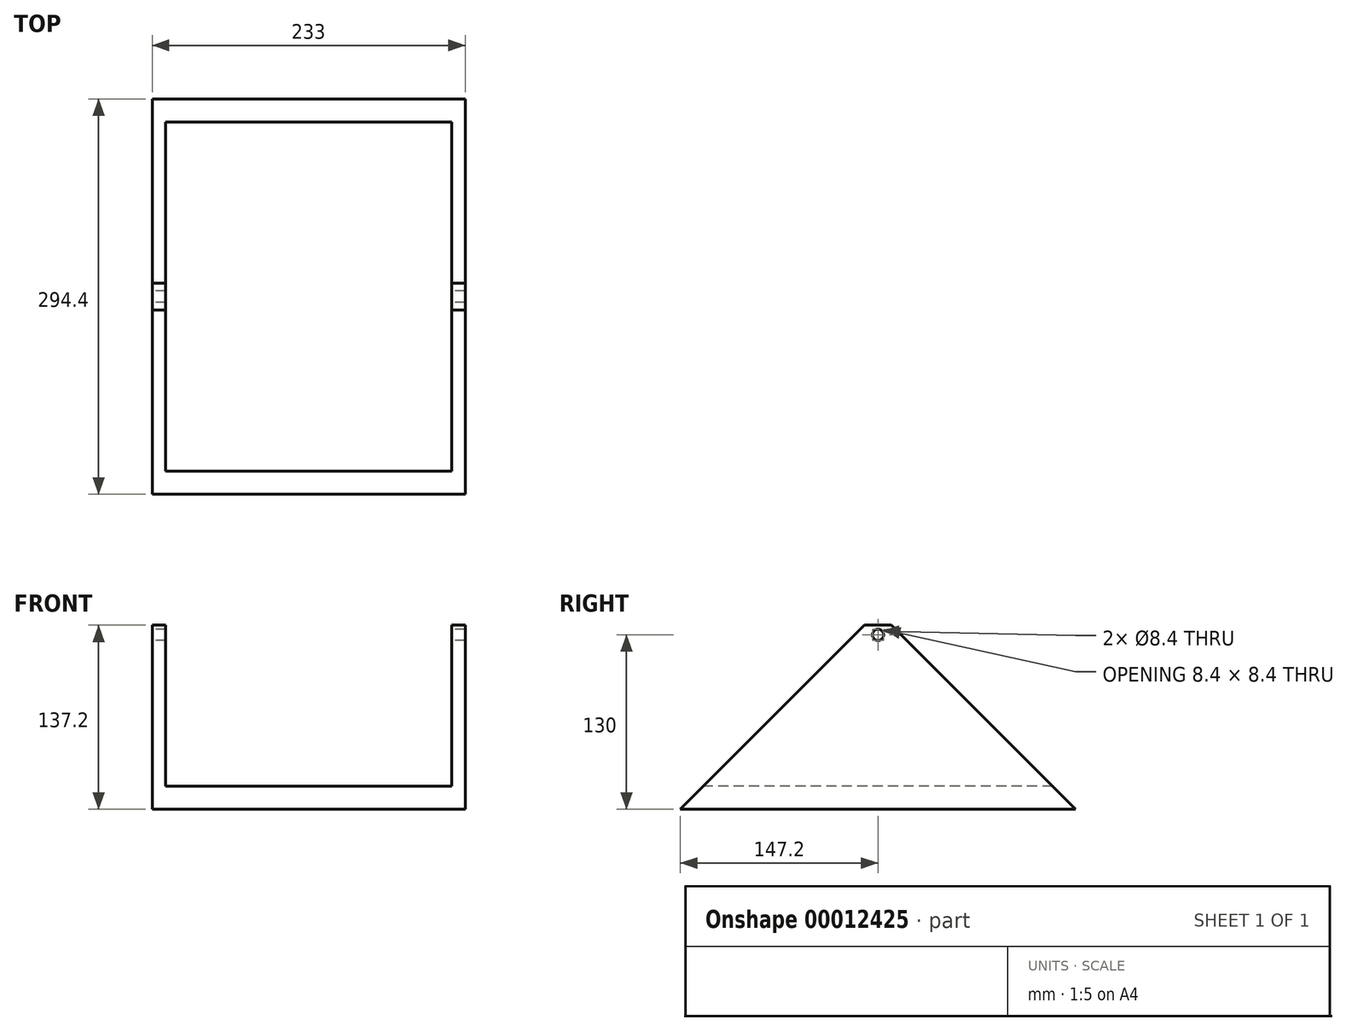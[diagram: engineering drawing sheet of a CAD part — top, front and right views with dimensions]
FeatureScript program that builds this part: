
annotation { "Feature Type Name" : "Feature", "Feature Type Description" : "" }
export const myFeature = defineFeature(function(context is Context, id is Id, definition is map)
    precondition{}
    {
        {
            var Q0;
            Q0=qCreatedBy(makeId("Right.planeOp"),FACE);
            var sketch = newSketch(context, id + "F0", { "sketchPlane" : qUnion([Q0])});
            skLineSegment(sketch, "E0", {"start": v(0, 0) * mm, "end": v(294.4, 0) * mm});
            skLineSegment(sketch, "E1", {"start": v(294.4, 0) * mm, "end": v(157.2, 137.2) * mm});
            skLineSegment(sketch, "E2", {"start": v(157.2, 137.2) * mm, "end": v(137.2, 137.2) * mm});
            skLineSegment(sketch, "E3", {"start": v(137.2, 137.2) * mm, "end": v(0, 0) * mm});
            skLineSegment(sketch, "E4", {"start": v(147.2, 137.2) * mm, "end": v(147.2, 0) * mm, "construction": true});
            skCircle(sketch, "E5", {"center": v(147.2, 130) * mm, "radius": 4.2 * mm});
            skPoint(sketch, "E6", {"position": v(147.2, 134.2) * mm});
            skSolve(sketch);
        }
        {
            var Q0;
            Q0 = qSketchRegion(id + "F0", true);
            extrude(context, id + "F1", {"entities" : qUnion([Q0]), "depth" : 233 * mm});
        }
        {
            var Q0;
            Q0=makeQuery(id+"F1.opExtrude","SWEPT_FACE",FACE,{"disambiguationData":[OSD([sQuery(id+"F0.wireOp",EDGE,"E2")])]});
            var sketch = newSketch(context, id + "F2", { "sketchPlane" : qUnion([Q0])});
            skLineSegment(sketch, "E7", {"start": v(116.5, 137.2) * mm, "end": v(116.5, 157.2) * mm, "construction": true});
            skLineSegment(sketch, "E8.rect.bottom", {"start": v(10, 294.4) * mm, "end": v(223, 294.4) * mm});
            skLineSegment(sketch, "E8.rect.top", {"start": v(10, 0) * mm, "end": v(223, 0) * mm});
            skLineSegment(sketch, "E8.rect.left", {"start": v(10, 294.4) * mm, "end": v(10, 0) * mm});
            skLineSegment(sketch, "E8.rect.right", {"start": v(223, 294.4) * mm, "end": v(223, 0) * mm});
            skPoint(sketch, "E8.rect.middle", {"position": v(116.5, 147.2) * mm});
            skSolve(sketch);
        }
        {
            var Q0;
            Q0 = qSketchRegion(id + "F2", true);
            extrude(context, id + "F3", {"entities" : qUnion([Q0]), "operationType" : NewBodyOperationType.REMOVE, "oppositeDirection" : true, "depth" : 120 * mm});
        }
    });
